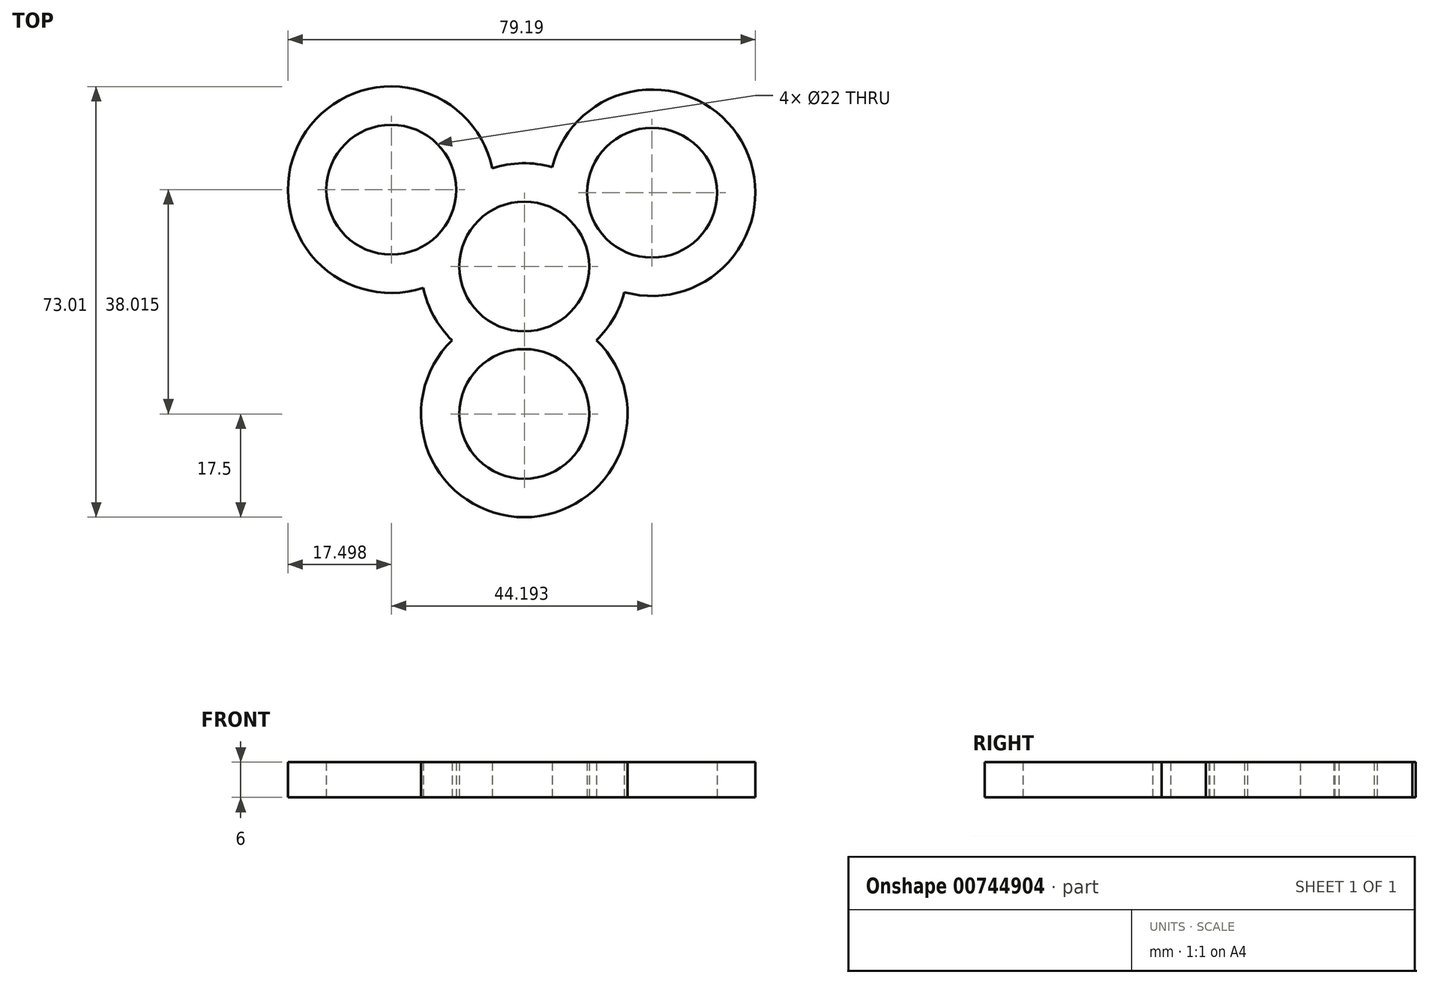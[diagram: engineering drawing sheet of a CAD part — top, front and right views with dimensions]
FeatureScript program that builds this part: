
annotation { "Feature Type Name" : "Feature", "Feature Type Description" : "" }
export const myFeature = defineFeature(function(context is Context, id is Id, definition is map)
    precondition{}
    {
        {
            var Q0;
            Q0=qCreatedBy(makeId("Top.planeOp"),FACE);
            var sketch = newSketch(context, id + "F0", { "sketchPlane" : qUnion([Q0])});
            skCircle(sketch, "E0", {"center": v(0, 0) * mm, "radius": 11 * mm});
            skCircle(sketch, "E1", {"center": v(0, -25) * mm, "radius": 11 * mm});
            skCircle(sketch, "E2", {"center": v(21.65, 12.5) * mm, "radius": 11 * mm});
            skCircle(sketch, "E3", {"center": v(-22.54, 13.01) * mm, "radius": 11 * mm});
            skArc(sketch, "E4", {"start": v(-5.42, 16.64) * mm, "mid": v(-37.7, 21.76) * mm, "end": v(-17.12, -3.62) * mm});
            skArc(sketch, "E5", {"start": v(-12.25, -12.5) * mm, "mid": v(0, -42.5) * mm, "end": v(12.25, -12.5) * mm});
            skArc(sketch, "E6", {"start": v(-17.12, -3.62) * mm, "mid": v(-15.34, -8.42) * mm, "end": v(-12.25, -12.5) * mm});
            skArc(sketch, "E7.trimOffspring", {"start": v(4.7, 16.86) * mm, "mid": v(-0.38, 17.5) * mm, "end": v(-5.42, 16.64) * mm});
            skArc(sketch, "E8.trimOffspring", {"start": v(16.95, -4.36) * mm, "mid": v(36.8, 21.25) * mm, "end": v(4.7, 16.86) * mm});
            skArc(sketch, "E9.trimOffspring", {"start": v(12.25, -12.5) * mm, "mid": v(15.16, -8.75) * mm, "end": v(16.95, -4.36) * mm});
            skSolve(sketch);
        }
        {
            var Q0;
            Q0 = qSketchRegion(id + "F0", true);
            extrude(context, id + "F1", {"entities" : qUnion([Q0]), "depth" : 6 * mm, "offsetDistance" : 25 * mm});
        }
    });
